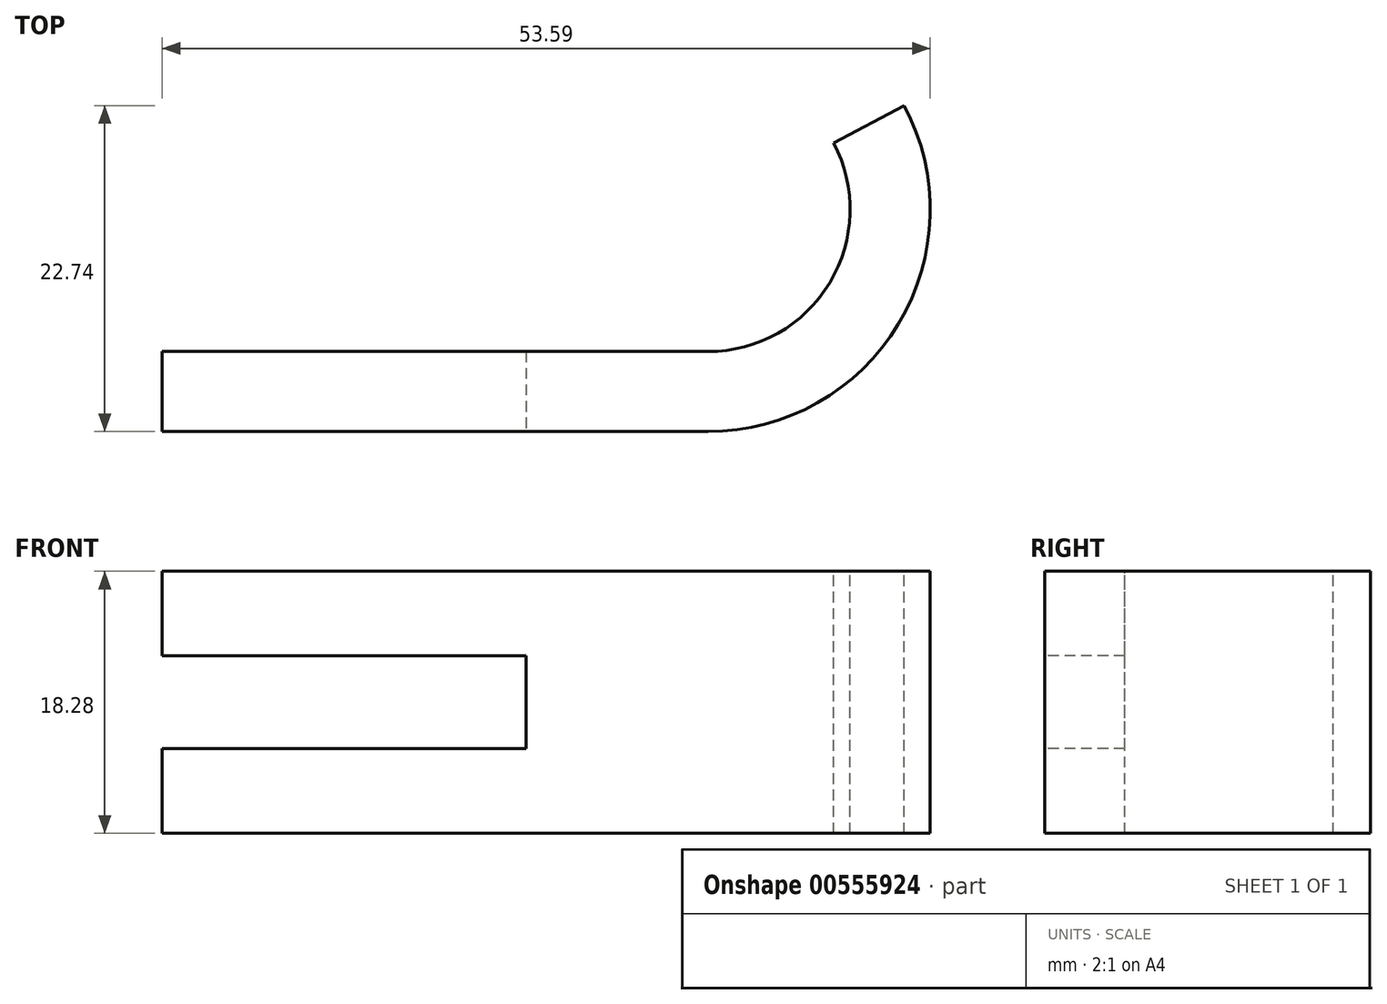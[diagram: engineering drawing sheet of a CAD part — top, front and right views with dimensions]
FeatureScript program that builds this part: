
annotation { "Feature Type Name" : "Feature", "Feature Type Description" : "" }
export const myFeature = defineFeature(function(context is Context, id is Id, definition is map)
    precondition{}
    {
        {
            var Q0;
            Q0=qCreatedBy(makeId("Top.planeOp"),FACE);
            var sketch = newSketch(context, id + "F0", { "sketchPlane" : qUnion([Q0])});
            skLineSegment(sketch, "E0", {"start": v(0, 0) * mm, "end": v(38.1, 0) * mm});
            skFitSpline(sketch, "E1", {"points": [v(51.4, 0) * mm, v(51.74, 15.37) * mm, v(45.9, 37.8) * mm, v(73.53, 59.31) * mm, v(111.33, 19.98) * mm, v(163.27, -43.95) * mm, v(195.54, -44.56) * mm, v(197.69, -31.35) * mm, v(183.55, -24.28) * mm, v(176.48, -34.73) * mm], "startDerivative": vector(-30.11, 895.48) * mm, "endDerivative": vector(-12.45, -261.55) * mm});
            skArc(sketch, "E2", {"start": v(38.1, 0) * mm, "mid": v(48.98, 6.15) * mm, "end": v(49.32, 18.65) * mm});
            skSolve(sketch);
        }
        {
            var Q0;
            Q0=qCreatedBy(makeId("Right.planeOp"),FACE);
            var sketch = newSketch(context, id + "F1", { "sketchPlane" : qUnion([Q0])});
            skLineSegment(sketch, "E3.bottom", {"start": v(2.8, -9.14) * mm, "end": v(-2.8, -9.14) * mm});
            skLineSegment(sketch, "E3.top", {"start": v(2.8, 9.14) * mm, "end": v(-2.8, 9.14) * mm});
            skLineSegment(sketch, "E3.left", {"start": v(2.8, -9.14) * mm, "end": v(2.8, 9.14) * mm});
            skLineSegment(sketch, "E3.right", {"start": v(-2.8, -9.14) * mm, "end": v(-2.8, 9.14) * mm});
            skSolve(sketch);
        }
        {
            var Q0;
            Q0=makeQuery(id+"F1.imprint","IMPRINT",FACE,{"disambiguationData":[TD([[makeQuery(id+"F1.imprint","IMPRINT",EDGE,{"derivedFrom":sQuery(id+"F1.wireOp",EDGE,"E3.bottom")}),-1.0]])]});
            var Q1;
            Q1=sQuery(id+"F0.wireOp",EDGE,"E0");
            var Q2;
            Q2=sQuery(id+"F0.wireOp",EDGE,"E2");
            var Q3;
            Q3=sQuery(id+"F0.wireOp",EDGE,"E1");
            sweep(context, id + "F2", {"profiles" : qUnion([Q0]), "path" : qUnion([Q1, Q2, Q3])});
        }
        {
            var Q0;
            Q0=makeQuery(id+"F2.opSweep","CAP_FACE",FACE,{"disambiguationData":[OSD([sQuery(id+"F0.wireOp",VERTEX,"E0.start"),sQuery(id+"F1.wireOp",EDGE,"E3.bottom"),sQuery(id+"F1.wireOp",EDGE,"E3.top"),sQuery(id+"F1.wireOp",EDGE,"E3.left"),sQuery(id+"F1.wireOp",EDGE,"E3.right")])],"isStart":true});
            var sketch = newSketch(context, id + "F3", { "sketchPlane" : qUnion([Q0])});
            skLineSegment(sketch, "E4.bottom", {"start": v(-2.8, -3.24) * mm, "end": v(2.8, -3.24) * mm});
            skLineSegment(sketch, "E4.top", {"start": v(-2.8, 3.24) * mm, "end": v(2.8, 3.24) * mm});
            skLineSegment(sketch, "E4.left", {"start": v(-2.8, -3.24) * mm, "end": v(-2.8, 3.24) * mm});
            skLineSegment(sketch, "E4.right", {"start": v(2.8, -3.24) * mm, "end": v(2.8, 3.24) * mm});
            skSolve(sketch);
        }
        {
            var Q0;
            Q0=makeQuery(id+"F3.imprint","IMPRINT",FACE,{"disambiguationData":[TD([[makeQuery(id+"F3.imprint","IMPRINT",EDGE,{"derivedFrom":sQuery(id+"F3.wireOp",EDGE,"E4.bottom")}),1.0]])]});
            extrude(context, id + "F4", {"entities" : qUnion([Q0]), "operationType" : NewBodyOperationType.REMOVE, "oppositeDirection" : true, "depth" : 25.4 * mm, "offsetDistance" : 25.4 * mm});
        }
    });
